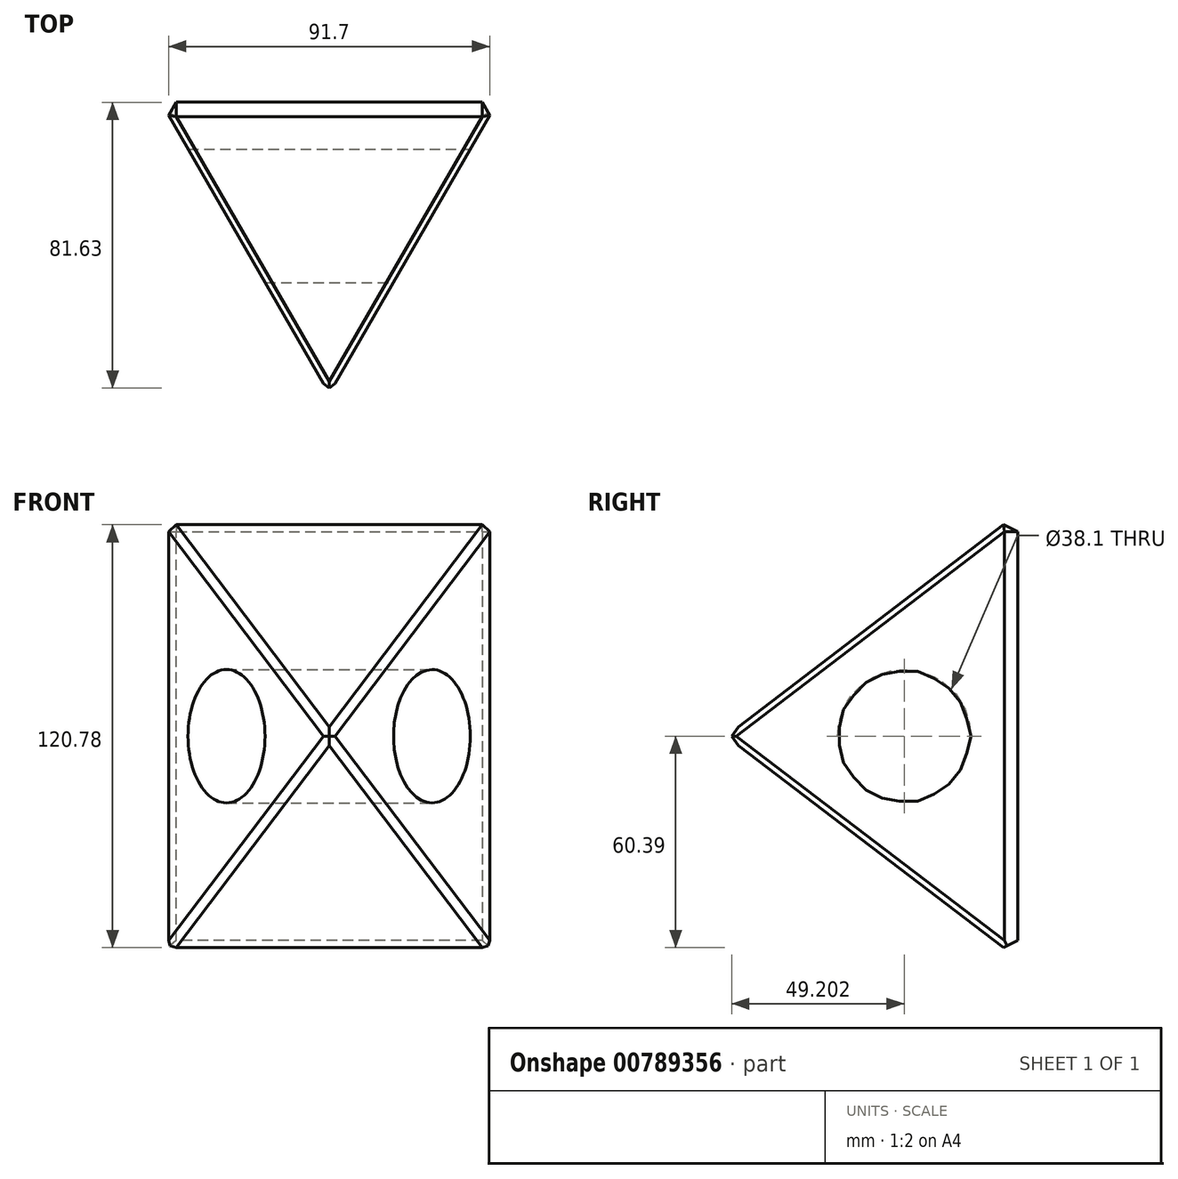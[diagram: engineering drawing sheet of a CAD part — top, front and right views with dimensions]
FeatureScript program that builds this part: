
annotation { "Feature Type Name" : "Feature", "Feature Type Description" : "" }
export const myFeature = defineFeature(function(context is Context, id is Id, definition is map)
    precondition{}
    {
        {
            var Q0;
            Q0=qCreatedBy(makeId("Top.planeOp"),FACE);
            var sketch = newSketch(context, id + "F0", { "sketchPlane" : qUnion([Q0])});
            skCircle(sketch, "E0.cCircle", {"center": v(0, 0) * mm, "radius": 27.74 * mm, "construction": true});
            skLineSegment(sketch, "E0.0", {"start": v(-48.05, 27.74) * mm, "end": v(48.05, 27.74) * mm});
            skLineSegment(sketch, "E0.1", {"start": v(48.05, 27.74) * mm, "end": v(0, -55.49) * mm});
            skLineSegment(sketch, "E0.2", {"start": v(0, -55.49) * mm, "end": v(-48.05, 27.74) * mm});
            skPoint(sketch, "E0.0.midPoint", {"position": v(0, 27.74) * mm});
            skSolve(sketch);
        }
        {
            var Q0;
            Q0=makeQuery(id+"F0.imprint","IMPRINT",FACE,{"disambiguationData":[TD([[makeQuery(id+"F0.imprint","IMPRINT",EDGE,{"derivedFrom":sQuery(id+"F0.wireOp",EDGE,"E0.0")}),-1.0]])]});
            extrude(context, id + "F1", {"entities" : qUnion([Q0]), "depth" : 127 * mm, "offsetDistance" : 25.4 * mm});
        }
        {
            var Q0;
            Q0=qCreatedBy(makeId("Right.planeOp"),FACE);
            var sketch = newSketch(context, id + "F2", { "sketchPlane" : qUnion([Q0])});
            skLineSegment(sketch, "E1.0", {"start": v(27.74, 127) * mm, "end": v(27.74, 0) * mm});
            skLineSegment(sketch, "E2.0", {"start": v(-55.49, 127) * mm, "end": v(27.74, 127) * mm});
            skLineSegment(sketch, "E3.0", {"start": v(-55.49, 127) * mm, "end": v(-55.49, 0) * mm});
            skLineSegment(sketch, "E4.0", {"start": v(-55.49, 0) * mm, "end": v(27.74, 0) * mm});
            skLineSegment(sketch, "E5", {"start": v(27.74, 0) * mm, "end": v(-55.49, 63.5) * mm});
            skLineSegment(sketch, "E6", {"start": v(-55.49, 63.5) * mm, "end": v(27.74, 127) * mm});
            skSolve(sketch);
        }
        {
            var Q0;
            {var subQ0=sQuery(id+"F2.wireOp",EDGE,"E4.0");Q0=makeQuery(id+"F2.imprint","IMPRINT",FACE,{"disambiguationData":[TD([[makeQuery(id+"F2.imprint","IMPRINT",EDGE,{"derivedFrom":subQ0}),1.0]])]});}
            var Q1;
            {var subQ0=sQuery(id+"F2.wireOp",EDGE,"E2.0");Q1=makeQuery(id+"F2.imprint","IMPRINT",FACE,{"disambiguationData":[TD([[makeQuery(id+"F2.imprint","IMPRINT",EDGE,{"derivedFrom":subQ0}),-1.0]])]});}
            extrude(context, id + "F3", {"entities" : qUnion([Q0, Q1]), "operationType" : NewBodyOperationType.REMOVE, "endBound" : BoundingType.THROUGH_ALL, "oppositeDirection" : true, "depth" : 25.4 * mm, "offsetDistance" : 25.4 * mm, "hasSecondDirection" : true, "secondDirectionBound" : SecondDirectionBoundingType.THROUGH_ALL, "secondDirectionOppositeDirection" : false, "secondDirectionDepth" : 25.4 * mm});
        }
        {
            var Q0;
            Q0=qCreatedBy(makeId("Right.planeOp"),FACE);
            var sketch = newSketch(context, id + "F4", { "sketchPlane" : qUnion([Q0])});
            skLineSegment(sketch, "E7.0", {"start": v(27.74, 127) * mm, "end": v(-55.49, 63.5) * mm});
            skLineSegment(sketch, "E8.0", {"start": v(-55.49, 63.5) * mm, "end": v(27.74, 0) * mm});
            skCircle(sketch, "E9", {"center": v(-4.69, 63.5) * mm, "radius": 19.05 * mm});
            skSolve(sketch);
        }
        {
            var Q0;
            Q0 = qSketchRegion(id + "F4", true);
            extrude(context, id + "F5", {"entities" : qUnion([Q0]), "operationType" : NewBodyOperationType.REMOVE, "endBound" : BoundingType.THROUGH_ALL, "oppositeDirection" : true, "depth" : 25.4 * mm, "offsetDistance" : 25.4 * mm, "hasSecondDirection" : true, "secondDirectionBound" : SecondDirectionBoundingType.THROUGH_ALL, "secondDirectionOppositeDirection" : false, "secondDirectionDepth" : 25.4 * mm});
        }
        {
            var Q0;
            Q0=qCreatedBy(makeId("Right.planeOp"),FACE);
            var sketch = newSketch(context, id + "F6", { "sketchPlane" : qUnion([Q0])});
            skPoint(sketch, "E10.0", {"position": v(-55.49, 63.5) * mm});
            skLineSegment(sketch, "E11", {"start": v(-55.49, 63.5) * mm, "end": v(-6.94, 63.5) * mm});
            skSolve(sketch);
        }
        {
            var Q0;
            Q0=makeQuery(id+"F3.boolean.opBoolean","INTERSECT",EDGE,{"derivedFrom":[makeQuery(id+"F1.opExtrude","SWEPT_FACE",FACE,{"disambiguationData":[OSD([sQuery(id+"F0.wireOp",EDGE,"E0.1")])]}),makeQuery(id+"F3.opExtrude","SWEPT_FACE",FACE,{"disambiguationData":[OSD([sQuery(id+"F2.wireOp",EDGE,"E6")])]})]});
            var Q1;
            Q1=makeQuery(id+"F3.boolean.opBoolean","INTERSECT",EDGE,{"derivedFrom":[makeQuery(id+"F1.opExtrude","SWEPT_FACE",FACE,{"disambiguationData":[OSD([sQuery(id+"F0.wireOp",EDGE,"E0.2")])]}),makeQuery(id+"F3.opExtrude","SWEPT_FACE",FACE,{"disambiguationData":[OSD([sQuery(id+"F2.wireOp",EDGE,"E6")])]})]});
            var Q2;
            Q2=makeQuery(id+"F3.boolean.opBoolean","MERGE",EDGE,{"derivedFrom":[makeQuery(id+"F1.opExtrude","CAP_EDGE",EDGE,{"disambiguationData":[OSD([sQuery(id+"F0.wireOp",EDGE,"E0.0")])],"isStart":false}),makeQuery(id+"F3.opExtrude","SWEPT_EDGE",EDGE,{"disambiguationData":[OSD([sQuery(id+"F2.wireOp",EDGE,"E1.0"),sQuery(id+"F2.wireOp",EDGE,"E2.0"),sQuery(id+"F2.wireOp",EDGE,"E6")])]})]});
            var Q3;
            Q3=makeQuery(id+"F1.opExtrude","SWEPT_EDGE",EDGE,{"disambiguationData":[OSD([sQuery(id+"F0.wireOp",EDGE,"E0.0"),sQuery(id+"F0.wireOp",EDGE,"E0.2")])]});
            var Q4;
            Q4=makeQuery(id+"F1.opExtrude","SWEPT_EDGE",EDGE,{"disambiguationData":[OSD([sQuery(id+"F0.wireOp",EDGE,"E0.0"),sQuery(id+"F0.wireOp",EDGE,"E0.1")])]});
            var Q5;
            Q5=makeQuery(id+"F3.boolean.opBoolean","MERGE",EDGE,{"derivedFrom":[makeQuery(id+"F1.opExtrude","CAP_EDGE",EDGE,{"disambiguationData":[OSD([sQuery(id+"F0.wireOp",EDGE,"E0.0")])],"isStart":true}),makeQuery(id+"F3.opExtrude","SWEPT_EDGE",EDGE,{"disambiguationData":[OSD([sQuery(id+"F2.wireOp",EDGE,"E1.0"),sQuery(id+"F2.wireOp",EDGE,"E4.0"),sQuery(id+"F2.wireOp",EDGE,"E5")])]})]});
            chamfer(context, id + "F7", {"entities" : qUnion([Q0, Q1, Q2, Q3, Q4, Q5]), "width" : 2.54 * mm, "tangentPropagation" : true});
        }
        {
            var Q0;
            Q0=makeQuery(id+"F3.boolean.opBoolean","INTERSECT",EDGE,{"derivedFrom":[makeQuery(id+"F1.opExtrude","SWEPT_FACE",FACE,{"disambiguationData":[OSD([sQuery(id+"F0.wireOp",EDGE,"E0.2")])]}),makeQuery(id+"F3.opExtrude","SWEPT_FACE",FACE,{"disambiguationData":[OSD([sQuery(id+"F2.wireOp",EDGE,"E5")])]})]});
            var Q1;
            Q1=makeQuery(id+"F3.boolean.opBoolean","INTERSECT",EDGE,{"derivedFrom":[makeQuery(id+"F1.opExtrude","SWEPT_FACE",FACE,{"disambiguationData":[OSD([sQuery(id+"F0.wireOp",EDGE,"E0.1")])]}),makeQuery(id+"F3.opExtrude","SWEPT_FACE",FACE,{"disambiguationData":[OSD([sQuery(id+"F2.wireOp",EDGE,"E5")])]})]});
            chamfer(context, id + "F8", {"entities" : qUnion([Q0, Q1]), "width" : 2.54 * mm, "tangentPropagation" : true});
        }
    });
